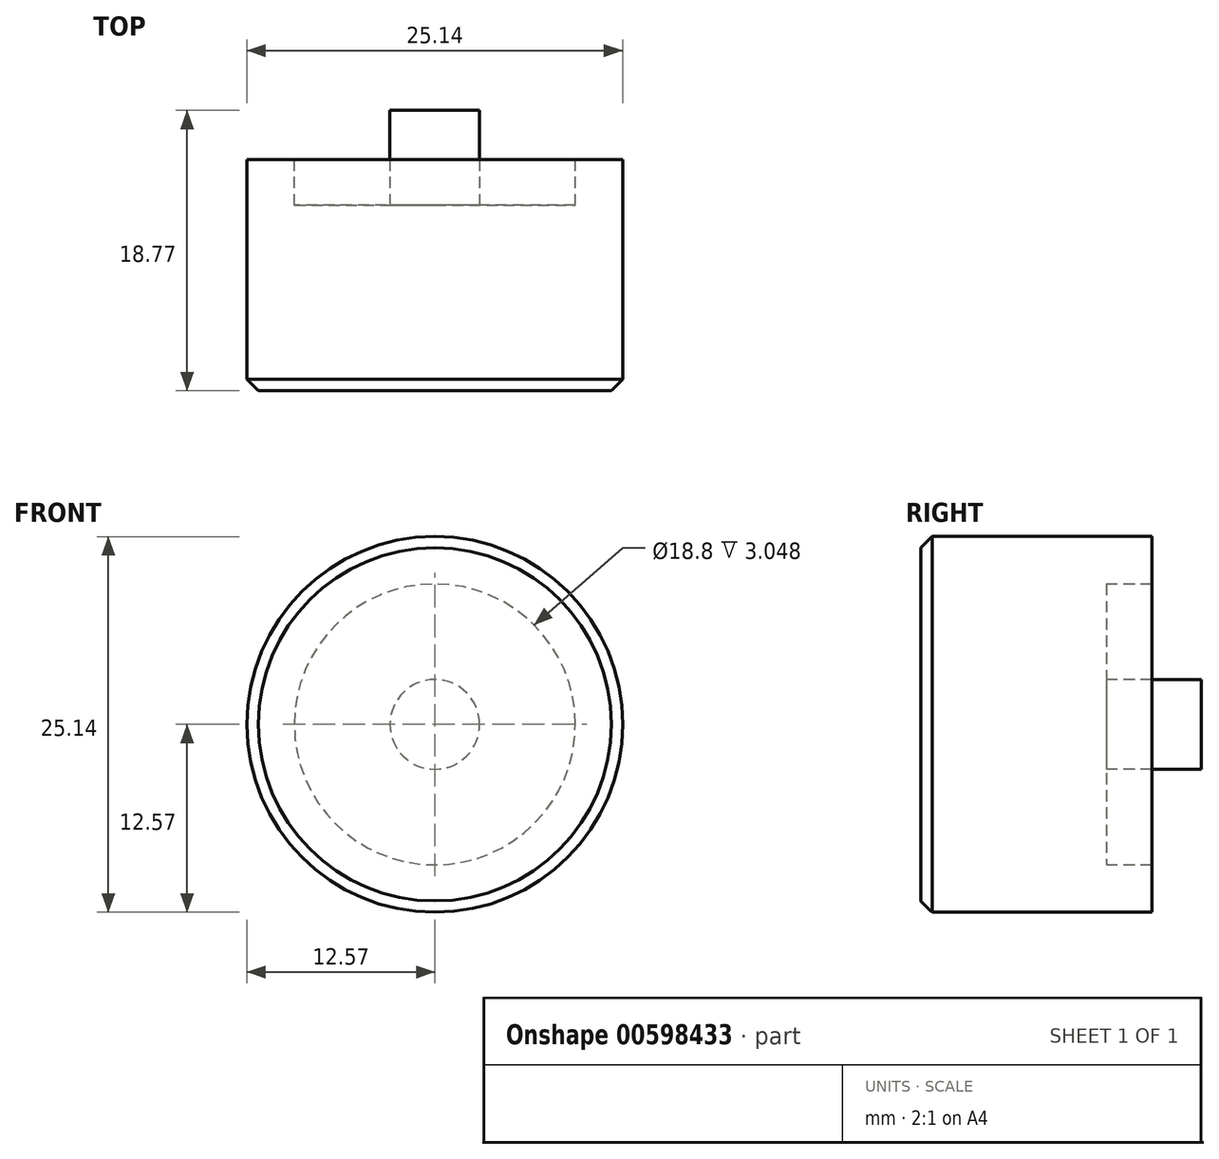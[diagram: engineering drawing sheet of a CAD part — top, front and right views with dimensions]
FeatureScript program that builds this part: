
annotation { "Feature Type Name" : "Feature", "Feature Type Description" : "" }
export const myFeature = defineFeature(function(context is Context, id is Id, definition is map)
    precondition{}
    {
        {
            var Q0;
            Q0=qCreatedBy(makeId("Front.planeOp"),FACE);
            var sketch = newSketch(context, id + "F0", { "sketchPlane" : qUnion([Q0])});
            skCircle(sketch, "E0", {"center": v(0, 0) * mm, "radius": 12.57 * mm});
            skSolve(sketch);
        }
        {
            var Q0;
            Q0=makeQuery(id+"F0.imprint","IMPRINT",FACE,{"disambiguationData":[TD([[makeQuery(id+"F0.imprint","IMPRINT",EDGE,{"derivedFrom":sQuery(id+"F0.wireOp",EDGE,"E0")}),1.0]])]});
            extrude(context, id + "F1", {"entities" : qUnion([Q0]), "depth" : 15.47 * mm, "offsetDistance" : 25.4 * mm});
        }
        {
            var Q0;
            Q0=makeQuery(id+"F1.opExtrude","CAP_FACE",FACE,{"disambiguationData":[OSD([sQuery(id+"F0.wireOp",EDGE,"E0")])],"isStart":true});
            var sketch = newSketch(context, id + "F2", { "sketchPlane" : qUnion([Q0])});
            skCircle(sketch, "E1", {"center": v(0, 0) * mm, "radius": 9.4 * mm});
            skSolve(sketch);
        }
        {
            var Q0;
            Q0 = qSketchRegion(id + "F2", true);
            extrude(context, id + "F3", {"entities" : qUnion([Q0]), "operationType" : NewBodyOperationType.REMOVE, "oppositeDirection" : true, "depth" : 3.05 * mm, "offsetDistance" : 25.4 * mm});
        }
        {
            var Q0;
            Q0=makeQuery(id+"F1.opExtrude","CAP_EDGE",EDGE,{"disambiguationData":[OSD([sQuery(id+"F0.wireOp",EDGE,"E0")])],"isStart":false});
            chamfer(context, id + "F4", {"entities" : qUnion([Q0]), "width" : 0.76 * mm, "tangentPropagation" : true});
        }
        {
            var Q0;
            Q0=makeQuery(id+"F3.boolean.opBoolean","COPY",FACE,{"derivedFrom":makeQuery(id+"F3.opExtrude","CAP_FACE",FACE,{"disambiguationData":[OSD([sQuery(id+"F2.wireOp",EDGE,"E1")])],"isStart":false})});
            var sketch = newSketch(context, id + "F5", { "sketchPlane" : qUnion([Q0])});
            skCircle(sketch, "E2", {"center": v(0, 0) * mm, "radius": 3 * mm});
            skSolve(sketch);
        }
        {
            var Q0;
            Q0 = qSketchRegion(id + "F5", true);
            extrude(context, id + "F6", {"entities" : qUnion([Q0]), "operationType" : NewBodyOperationType.ADD, "depth" : 6.35 * mm, "offsetDistance" : 25.4 * mm});
        }
    });
